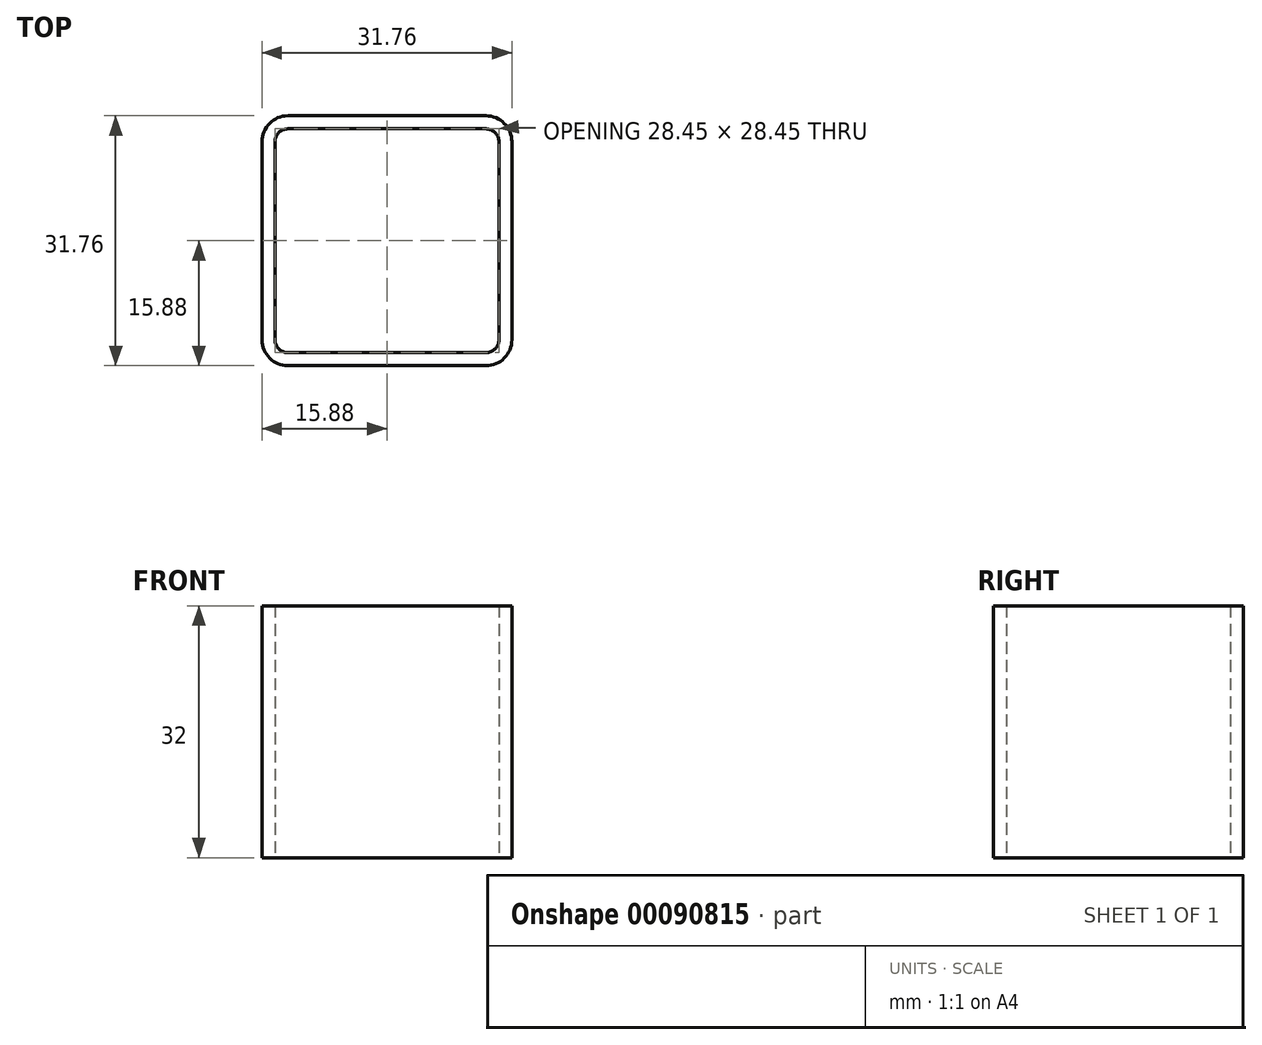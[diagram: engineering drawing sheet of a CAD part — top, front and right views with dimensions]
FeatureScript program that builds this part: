
annotation { "Feature Type Name" : "Feature", "Feature Type Description" : "" }
export const myFeature = defineFeature(function(context is Context, id is Id, definition is map)
    precondition{}
    {
        {
            var Q0;
            Q0=qCreatedBy(makeId("Top.planeOp"),FACE);
            var sketch = newSketch(context, id + "F0", { "sketchPlane" : qUnion([Q0])});
            skLineSegment(sketch, "E0.bottom", {"start": v(12.57, -15.88) * mm, "end": v(-12.57, -15.88) * mm});
            skLineSegment(sketch, "E0.top", {"start": v(12.57, 15.88) * mm, "end": v(-12.57, 15.88) * mm});
            skLineSegment(sketch, "E0.left", {"start": v(15.88, -12.57) * mm, "end": v(15.88, 12.57) * mm});
            skLineSegment(sketch, "E0.right", {"start": v(-15.88, -12.57) * mm, "end": v(-15.88, 12.57) * mm});
            skPoint(sketch, "E0.middle", {"position": v(0, 0) * mm});
            skPoint(sketch, "E1.visualSharp", {"position": v(-15.88, 15.87) * mm});
            skArc(sketch, "E1.filletArc", {"start": v(-12.57, 15.88) * mm, "mid": v(-14.9, 14.9) * mm, "end": v(-15.88, 12.57) * mm});
            skPoint(sketch, "E2.visualSharp", {"position": v(15.88, 15.88) * mm});
            skArc(sketch, "E2.filletArc", {"start": v(15.88, 12.57) * mm, "mid": v(14.9, 14.9) * mm, "end": v(12.57, 15.88) * mm});
            skPoint(sketch, "E3.visualSharp", {"position": v(15.87, -15.88) * mm});
            skArc(sketch, "E3.filletArc", {"start": v(12.57, -15.88) * mm, "mid": v(14.9, -14.9) * mm, "end": v(15.88, -12.57) * mm});
            skPoint(sketch, "E4.visualSharp", {"position": v(-15.88, -15.88) * mm});
            skArc(sketch, "E4.filletArc", {"start": v(-15.88, -12.57) * mm, "mid": v(-14.9, -14.9) * mm, "end": v(-12.57, -15.88) * mm});
            skLineSegment(sketch, "E5.0", {"start": v(12.57, 14.22) * mm, "end": v(-12.57, 14.22) * mm});
            skLineSegment(sketch, "E6.0", {"start": v(-14.22, -12.57) * mm, "end": v(-14.22, 12.57) * mm});
            skLineSegment(sketch, "E7.0", {"start": v(14.22, -12.57) * mm, "end": v(14.22, 12.57) * mm});
            skLineSegment(sketch, "E8.0", {"start": v(12.57, -14.22) * mm, "end": v(-12.57, -14.22) * mm});
            skArc(sketch, "E9.filletArc", {"start": v(-12.57, 14.22) * mm, "mid": v(-13.74, 13.74) * mm, "end": v(-14.22, 12.57) * mm});
            skArc(sketch, "E10.filletArc", {"start": v(14.22, 12.57) * mm, "mid": v(13.74, 13.74) * mm, "end": v(12.57, 14.22) * mm});
            skArc(sketch, "E11.filletArc", {"start": v(-14.22, -12.57) * mm, "mid": v(-13.74, -13.74) * mm, "end": v(-12.57, -14.22) * mm});
            skArc(sketch, "E12.filletArc", {"start": v(12.57, -14.22) * mm, "mid": v(13.74, -13.74) * mm, "end": v(14.22, -12.57) * mm});
            skSolve(sketch);
        }
        {
            assignVariable(context, id + "F1", {"name" : "L", "anyValue" : 32});
        }
        {
            var Q0;
            Q0=makeQuery(id+"F0.imprint","IMPRINT",FACE,{"disambiguationData":[TD([[makeQuery(id+"F0.imprint","IMPRINT",EDGE,{"derivedFrom":sQuery(id+"F0.wireOp",EDGE,"E0.bottom")}),-1.0]])]});
            extrude(context, id + "F2", {"entities" : qUnion([Q0]), "depth" : (getVariable(context, 'L')) * mm});
        }
        {
            var Q0;
            Q0=makeQuery(id+"F2.opExtrude","SWEPT_FACE",FACE,{"disambiguationData":[OSD([sQuery(id+"F0.wireOp",EDGE,"E0.bottom")])]});
            var sketch = newSketch(context, id + "F3", { "sketchPlane" : qUnion([Q0])});
            skPoint(sketch, "E13", {"position": v(0, 101.6) * mm});
            skPoint(sketch, "E13.positionSnap0", {"position": v(0, 0) * mm});
            skSolve(sketch);
        }
        {
            var Q0;
            {var subQ0=sQuery(id+"F0.wireOp",EDGE,"E0.bottom");Q0=makeQuery(id+"F3.imprint","IMPRINT",FACE,{"disambiguationData":[TD([[makeQuery(id+"F3.imprint","IMPRINT",EDGE,{"derivedFrom":makeQuery(id+"F2.opExtrude","CAP_EDGE",EDGE,{"disambiguationData":[OSD([subQ0])],"isStart":true})}),-1.0]])]});}
            var sketch = newSketch(context, id + "F4", { "sketchPlane" : qUnion([Q0])});
            skPoint(sketch, "E14", {"position": v(4.76, 685.8) * mm});
            skPoint(sketch, "E15", {"position": v(4.76, 228.6) * mm});
            skSolve(sketch);
        }
        {
            var Q0;
            Q0=makeQuery(id+"F2.opExtrude","SWEPT_FACE",FACE,{"disambiguationData":[OSD([sQuery(id+"F0.wireOp",EDGE,"E0.left")])]});
            var sketch = newSketch(context, id + "F5", { "sketchPlane" : qUnion([Q0])});
            skPoint(sketch, "E16", {"position": v(0, 101.6) * mm});
            skPoint(sketch, "E16.positionSnap0", {"position": v(0, 0) * mm});
            skSolve(sketch);
        }
        {
            var Q0;
            {var subQ0=sQuery(id+"F0.wireOp",EDGE,"E0.left");Q0=makeQuery(id+"F5.imprint","IMPRINT",FACE,{"disambiguationData":[TD([[makeQuery(id+"F5.imprint","IMPRINT",EDGE,{"derivedFrom":makeQuery(id+"F2.opExtrude","CAP_EDGE",EDGE,{"disambiguationData":[OSD([subQ0])],"isStart":true})}),1.0]])]});}
            var sketch = newSketch(context, id + "F6", { "sketchPlane" : qUnion([Q0])});
            skPoint(sketch, "E17", {"position": v(-4.76, 685.8) * mm});
            skPoint(sketch, "E18", {"position": v(-4.76, 228.6) * mm});
            skSolve(sketch);
        }
    });
